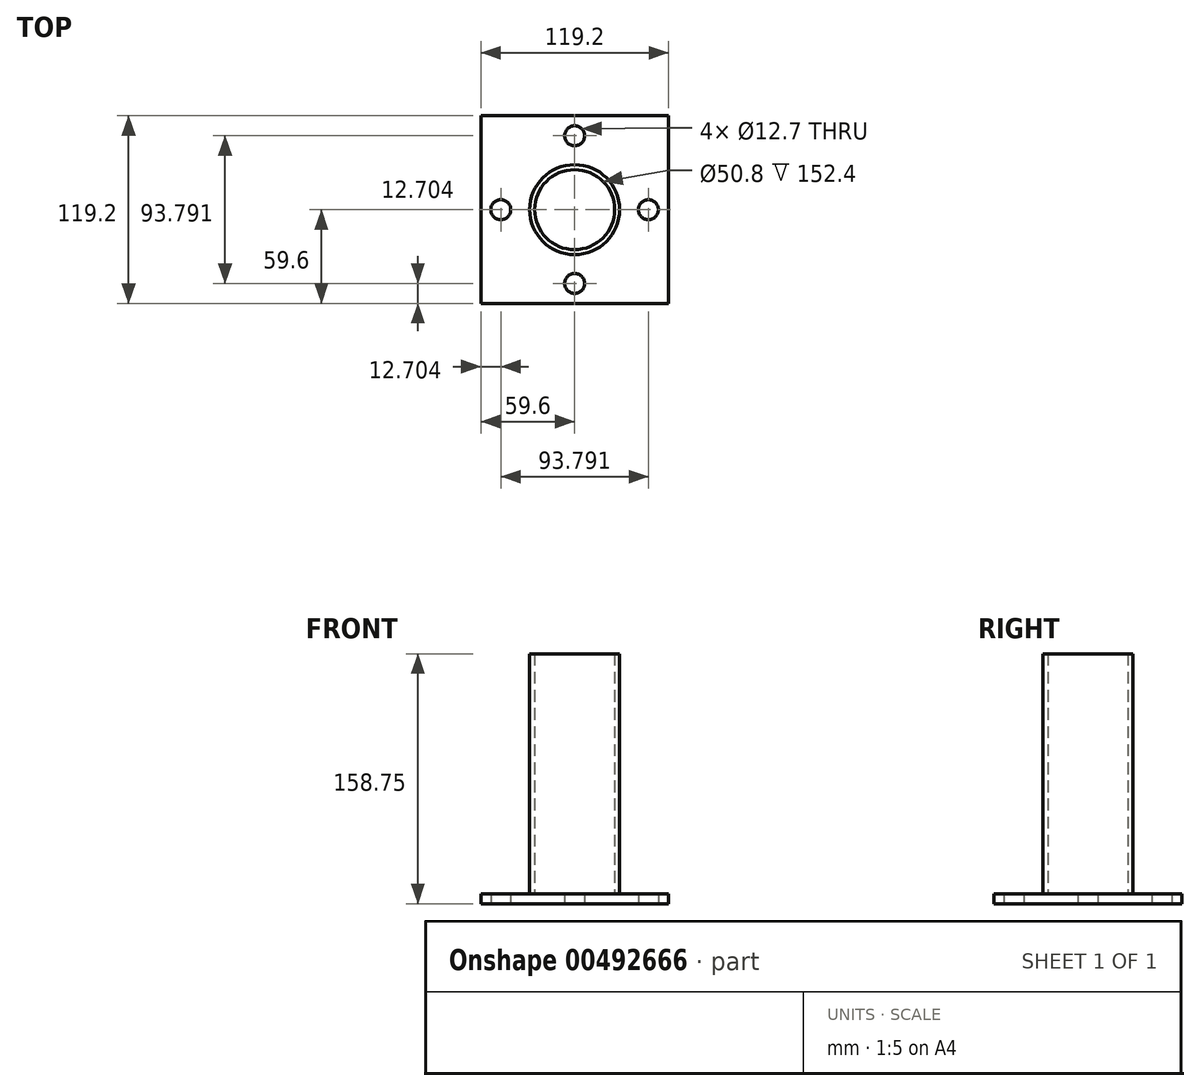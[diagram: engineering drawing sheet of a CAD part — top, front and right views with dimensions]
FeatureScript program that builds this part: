
annotation { "Feature Type Name" : "Feature", "Feature Type Description" : "" }
export const myFeature = defineFeature(function(context is Context, id is Id, definition is map)
    precondition{}
    {
        {
            var Q0;
            Q0=qCreatedBy(makeId("Top.planeOp"),FACE);
            var sketch = newSketch(context, id + "F0", { "sketchPlane" : qUnion([Q0])});
            skLineSegment(sketch, "E0.bottom", {"start": v(59.6, -59.6) * mm, "end": v(-59.6, -59.6) * mm});
            skLineSegment(sketch, "E0.top", {"start": v(59.6, 59.6) * mm, "end": v(-59.6, 59.6) * mm});
            skLineSegment(sketch, "E0.left", {"start": v(59.6, -59.6) * mm, "end": v(59.6, 59.6) * mm});
            skLineSegment(sketch, "E0.right", {"start": v(-59.6, -59.6) * mm, "end": v(-59.6, 59.6) * mm});
            skPoint(sketch, "E0.middle", {"position": v(0, 0) * mm});
            skLineSegment(sketch, "E1", {"start": v(0, 59.6) * mm, "end": v(0, -59.6) * mm, "construction": true});
            skLineSegment(sketch, "E2", {"start": v(-59.6, 0) * mm, "end": v(59.6, 0) * mm, "construction": true});
            skLineSegment(sketch, "E3", {"start": v(-52.97, 52.97) * mm, "end": v(-59.6, 59.6) * mm, "construction": true});
            skLineSegment(sketch, "E4", {"start": v(-59.6, 59.6) * mm, "end": v(59.6, -59.6) * mm, "construction": true});
            skLineSegment(sketch, "E5", {"start": v(-59.6, -59.6) * mm, "end": v(59.6, 59.6) * mm, "construction": true});
            skCircle(sketch, "E6", {"center": v(0, 46.9) * mm, "radius": 6.35 * mm});
            skCircle(sketch, "E7.MirrorC", {"center": v(0, -46.9) * mm, "radius": 6.35 * mm});
            skCircle(sketch, "E8.MirrorC", {"center": v(-46.9, 0) * mm, "radius": 6.35 * mm});
            skCircle(sketch, "E9.MirrorC", {"center": v(46.9, 0) * mm, "radius": 6.35 * mm});
            skSolve(sketch);
        }
        {
            var Q0;
            Q0 = qSketchRegion(id + "F0", true);
            extrude(context, id + "F1", {"entities" : qUnion([Q0]), "depth" : 6.35 * mm});
        }
        {
            var Q0;
            Q0=makeQuery(id+"F1.opExtrude","CAP_FACE",FACE,{"disambiguationData":[OSD([sQuery(id+"F0.wireOp",EDGE,"E0.bottom"),sQuery(id+"F0.wireOp",EDGE,"E0.top"),sQuery(id+"F0.wireOp",EDGE,"E0.left"),sQuery(id+"F0.wireOp",EDGE,"E0.right"),sQuery(id+"F0.wireOp",EDGE,"E6"),sQuery(id+"F0.wireOp",EDGE,"E7.MirrorC"),sQuery(id+"F0.wireOp",EDGE,"E8.MirrorC"),sQuery(id+"F0.wireOp",EDGE,"E9.MirrorC")])],"isStart":false});
            var sketch = newSketch(context, id + "F2", { "sketchPlane" : qUnion([Q0])});
            skCircle(sketch, "E10", {"center": v(0, 0) * mm, "radius": 28.58 * mm});
            skCircle(sketch, "E11", {"center": v(0, 0) * mm, "radius": 25.4 * mm});
            skSolve(sketch);
        }
        {
            var Q0;
            Q0 = qSketchRegion(id + "F2", true);
            extrude(context, id + "F3", {"entities" : qUnion([Q0]), "operationType" : NewBodyOperationType.ADD, "depth" : 152.4 * mm, "offsetDistance" : 25 * mm});
        }
    });
